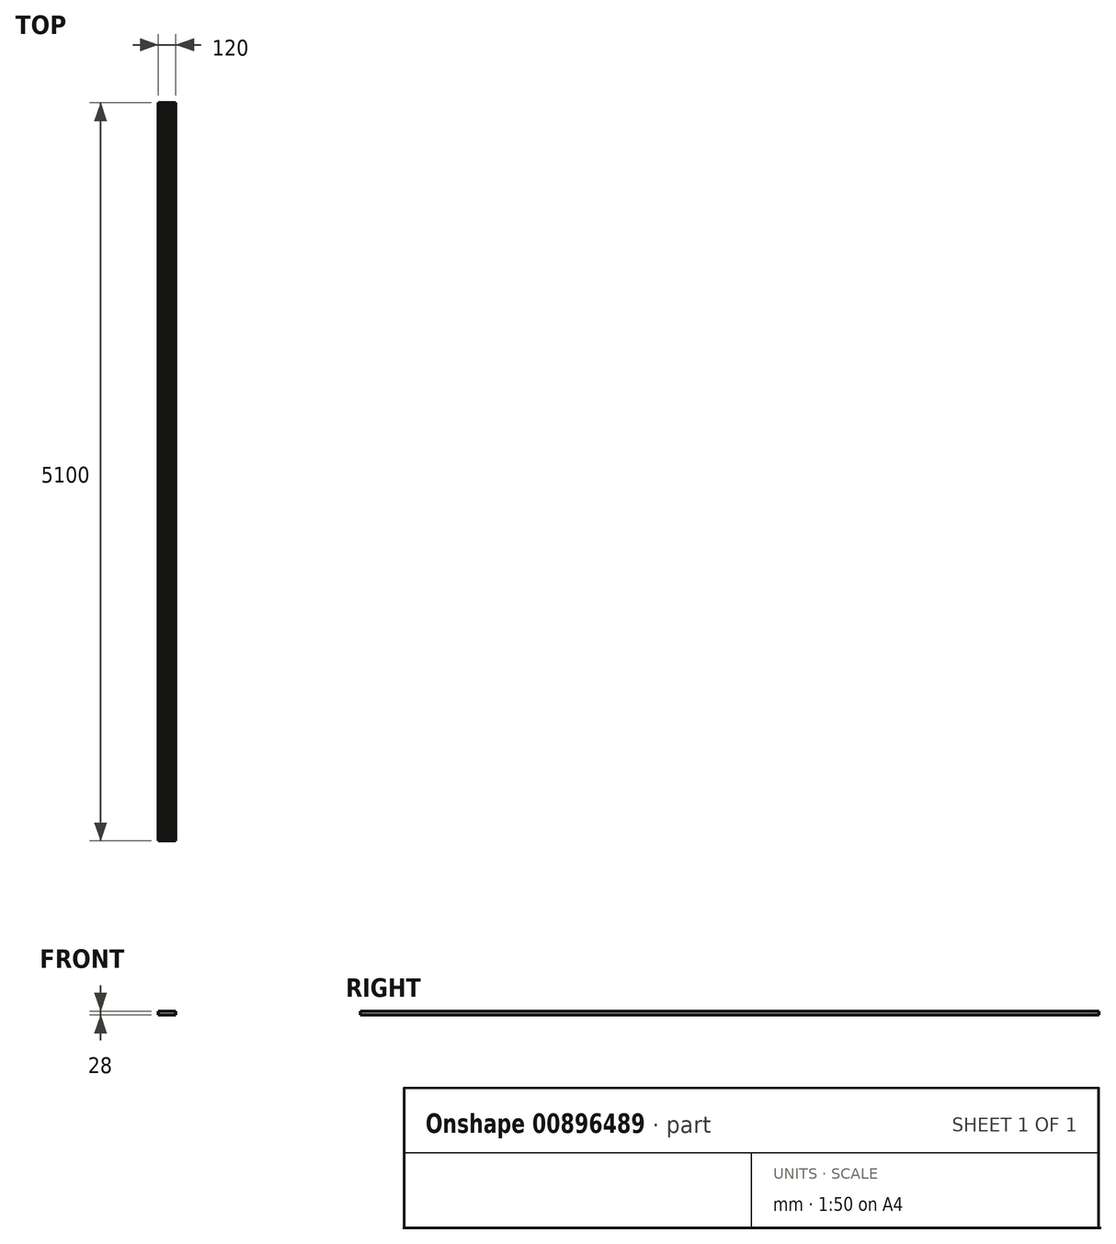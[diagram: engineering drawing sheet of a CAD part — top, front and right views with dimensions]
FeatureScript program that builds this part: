
annotation { "Feature Type Name" : "Feature", "Feature Type Description" : "" }
export const myFeature = defineFeature(function(context is Context, id is Id, definition is map)
    precondition{}
    {
        {
            var Q0;
            Q0=qCreatedBy(makeId("Top.planeOp"),FACE);
            var sketch = newSketch(context, id + "F0", { "sketchPlane" : qUnion([Q0])});
            skLineSegment(sketch, "E0.bottom", {"start": v(-306.56, -2536.04) * mm, "end": v(-186.56, -2536.04) * mm});
            skLineSegment(sketch, "E0.top", {"start": v(-306.56, 2563.96) * mm, "end": v(-186.56, 2563.96) * mm});
            skLineSegment(sketch, "E0.left", {"start": v(-306.56, -2536.04) * mm, "end": v(-306.56, 2563.96) * mm});
            skLineSegment(sketch, "E0.right", {"start": v(-186.56, -2536.04) * mm, "end": v(-186.56, 2563.96) * mm});
            skSolve(sketch);
        }
        {
            var Q0;
            Q0 = qSketchRegion(id + "F0", true);
            extrude(context, id + "F1", {"entities" : qUnion([Q0]), "depth" : 28 * mm, "offsetDistance" : 25 * mm});
        }
        {
            var Q0;
            Q0=makeQuery(id+"F1.opExtrude","CAP_EDGE",EDGE,{"disambiguationData":[OSD([sQuery(id+"F0.wireOp",EDGE,"E0.left")])],"isStart":false});
            var Q1;
            Q1=makeQuery(id+"F1.opExtrude","CAP_EDGE",EDGE,{"disambiguationData":[OSD([sQuery(id+"F0.wireOp",EDGE,"E0.right")])],"isStart":false});
            chamfer(context, id + "F2", {"entities" : qUnion([Q0, Q1]), "width" : 3 * mm, "tangentPropagation" : true});
        }
        {
            var Q0;
            Q0=makeQuery(id+"F1.opExtrude","SWEPT_FACE",FACE,{"disambiguationData":[OSD([sQuery(id+"F0.wireOp",EDGE,"E0.bottom")])]});
            var sketch = newSketch(context, id + "F3", { "sketchPlane" : qUnion([Q0])});
            skLineSegment(sketch, "E1", {"start": v(-306.56, 0) * mm, "end": v(-306.56, 25) * mm});
            skLineSegment(sketch, "E2", {"start": v(-306.56, 25) * mm, "end": v(-303.56, 28) * mm});
            skLineSegment(sketch, "E3", {"start": v(-303.56, 28) * mm, "end": v(-293.56, 28) * mm});
            skLineSegment(sketch, "E4", {"start": v(-290.56, 25) * mm, "end": v(-293.56, 28) * mm});
            skLineSegment(sketch, "E5", {"start": v(-290.56, 25) * mm, "end": v(-285.56, 25) * mm});
            skLineSegment(sketch, "E6", {"start": v(-285.56, 25) * mm, "end": v(-282.56, 28) * mm});
            skLineSegment(sketch, "E7", {"start": v(-282.56, 28) * mm, "end": v(-272.56, 28) * mm});
            skLineSegment(sketch, "E8", {"start": v(-272.56, 28) * mm, "end": v(-269.56, 25) * mm});
            skLineSegment(sketch, "E9", {"start": v(-269.56, 25) * mm, "end": v(-265.56, 25) * mm});
            skLineSegment(sketch, "E10", {"start": v(-262.56, 28) * mm, "end": v(-265.56, 25) * mm});
            skLineSegment(sketch, "E11", {"start": v(-262.56, 28) * mm, "end": v(-252.56, 28) * mm});
            skLineSegment(sketch, "E12", {"start": v(-252.56, 28) * mm, "end": v(-249.56, 25) * mm});
            skLineSegment(sketch, "E13", {"start": v(-249.56, 25) * mm, "end": v(-244.56, 25) * mm});
            skLineSegment(sketch, "E14", {"start": v(-241.56, 28) * mm, "end": v(-244.56, 25) * mm});
            skLineSegment(sketch, "E15", {"start": v(-241.56, 28) * mm, "end": v(-231.56, 28) * mm});
            skLineSegment(sketch, "E16", {"start": v(-231.56, 28) * mm, "end": v(-228.56, 25) * mm});
            skLineSegment(sketch, "E17", {"start": v(-228.56, 25) * mm, "end": v(-223.56, 25) * mm});
            skLineSegment(sketch, "E18", {"start": v(-220.56, 28) * mm, "end": v(-223.56, 25) * mm});
            skLineSegment(sketch, "E19", {"start": v(-220.56, 28) * mm, "end": v(-210.56, 28) * mm});
            skLineSegment(sketch, "E20", {"start": v(-210.56, 28) * mm, "end": v(-207.56, 25) * mm});
            skLineSegment(sketch, "E21", {"start": v(-207.56, 25) * mm, "end": v(-202.56, 25) * mm});
            skLineSegment(sketch, "E22", {"start": v(-199.56, 28) * mm, "end": v(-202.56, 25) * mm});
            skLineSegment(sketch, "E23", {"start": v(-199.56, 28) * mm, "end": v(-189.56, 28) * mm});
            skLineSegment(sketch, "E24", {"start": v(-189.56, 28) * mm, "end": v(-186.56, 25) * mm});
            skLineSegment(sketch, "E25", {"start": v(-186.56, 25) * mm, "end": v(-186.56, 0) * mm});
            skLineSegment(sketch, "E26", {"start": v(-186.56, 0) * mm, "end": v(-306.56, 0) * mm});
            skLineSegment(sketch, "E27", {"start": v(-293.56, 28) * mm, "end": v(-282.56, 28) * mm});
            skLineSegment(sketch, "E28", {"start": v(-272.56, 28) * mm, "end": v(-262.56, 28) * mm});
            skLineSegment(sketch, "E29", {"start": v(-252.56, 28) * mm, "end": v(-241.56, 28) * mm});
            skLineSegment(sketch, "E30", {"start": v(-231.56, 28) * mm, "end": v(-220.56, 28) * mm});
            skLineSegment(sketch, "E31", {"start": v(-210.56, 28) * mm, "end": v(-199.56, 28) * mm});
            skSolve(sketch);
        }
        {
            var Q0;
            Q0=makeQuery(id+"F3.imprint","IMPRINT",FACE,{"disambiguationData":[TD([[makeQuery(id+"F3.imprint","IMPRINT",EDGE,{"derivedFrom":sQuery(id+"F3.wireOp",EDGE,"E4")}),-1.0]])]});
            var Q1;
            Q1=makeQuery(id+"F3.imprint","IMPRINT",FACE,{"disambiguationData":[TD([[makeQuery(id+"F3.imprint","IMPRINT",EDGE,{"derivedFrom":sQuery(id+"F3.wireOp",EDGE,"E8")}),1.0]])]});
            var Q2;
            Q2=makeQuery(id+"F3.imprint","IMPRINT",FACE,{"disambiguationData":[TD([[makeQuery(id+"F3.imprint","IMPRINT",EDGE,{"derivedFrom":sQuery(id+"F3.wireOp",EDGE,"E12")}),1.0]])]});
            var Q3;
            Q3=makeQuery(id+"F3.imprint","IMPRINT",FACE,{"disambiguationData":[TD([[makeQuery(id+"F3.imprint","IMPRINT",EDGE,{"derivedFrom":sQuery(id+"F3.wireOp",EDGE,"E16")}),1.0]])]});
            var Q4;
            Q4=makeQuery(id+"F3.imprint","IMPRINT",FACE,{"disambiguationData":[TD([[makeQuery(id+"F3.imprint","IMPRINT",EDGE,{"derivedFrom":sQuery(id+"F3.wireOp",EDGE,"E20")}),1.0]])]});
            extrude(context, id + "F4", {"entities" : qUnion([Q0, Q1, Q2, Q3, Q4]), "operationType" : NewBodyOperationType.REMOVE, "oppositeDirection" : true, "depth" : 5100 * mm, "offsetDistance" : 25 * mm});
        }
    });
